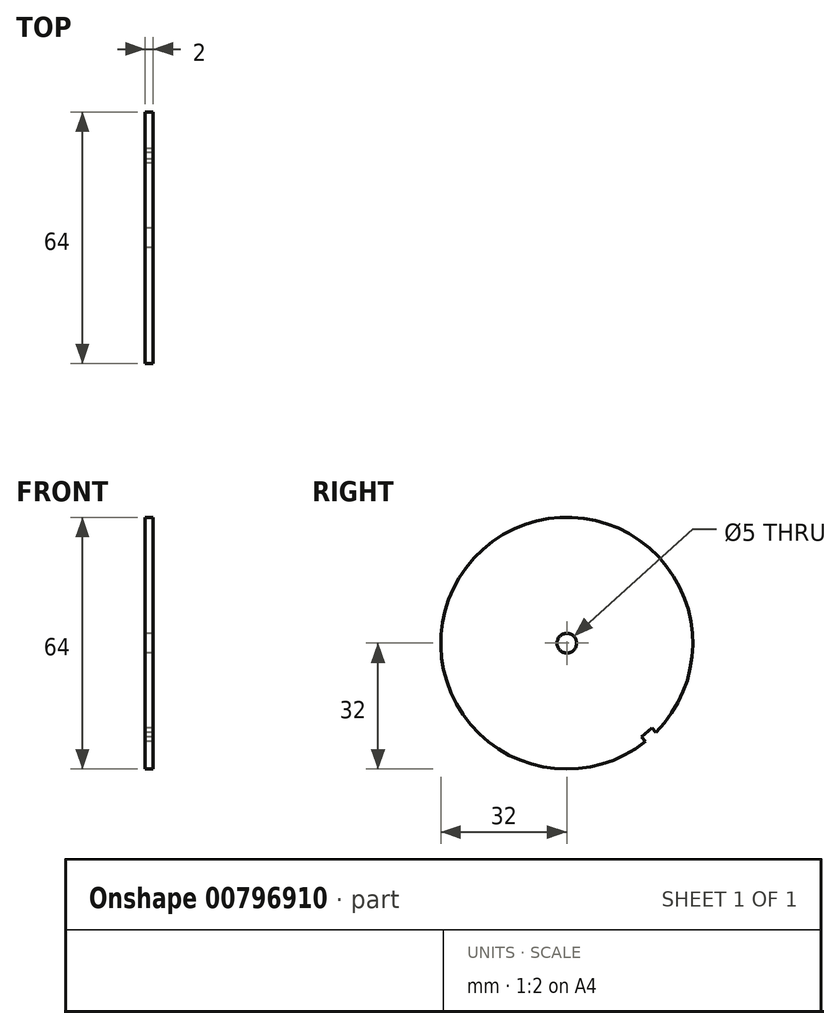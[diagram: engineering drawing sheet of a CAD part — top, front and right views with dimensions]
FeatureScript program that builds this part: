
annotation { "Feature Type Name" : "Feature", "Feature Type Description" : "" }
export const myFeature = defineFeature(function(context is Context, id is Id, definition is map)
    precondition{}
    {
        {
            var Q0;
            Q0=qCreatedBy(makeId("Right.planeOp"),FACE);
            var sketch = newSketch(context, id + "F0", { "sketchPlane" : qUnion([Q0])});
            skArc(sketch, "E0", {"start": v(22.6, -22.65) * mm, "mid": v(-21.34, 23.85) * mm, "end": v(20, -24.98) * mm});
            skCircle(sketch, "E1", {"center": v(0, 0) * mm, "radius": 2.5 * mm});
            skLineSegment(sketch, "E2", {"start": v(22.6, -22.65) * mm, "end": v(21.6, -21.53) * mm});
            skLineSegment(sketch, "E3", {"start": v(21.6, -21.53) * mm, "end": v(19, -23.86) * mm});
            skLineSegment(sketch, "E4", {"start": v(19, -23.86) * mm, "end": v(20, -24.98) * mm});
            skSolve(sketch);
        }
        {
            var Q0;
            Q0=makeQuery(id+"F0.imprint","IMPRINT",FACE,{"disambiguationData":[TD([[makeQuery(id+"F0.imprint","IMPRINT",EDGE,{"derivedFrom":sQuery(id+"F0.wireOp",EDGE,"E0")}),1.0]])]});
            extrude(context, id + "F1", {"entities" : qUnion([Q0]), "depth" : 2 * mm, "offsetDistance" : 25 * mm});
        }
    });
